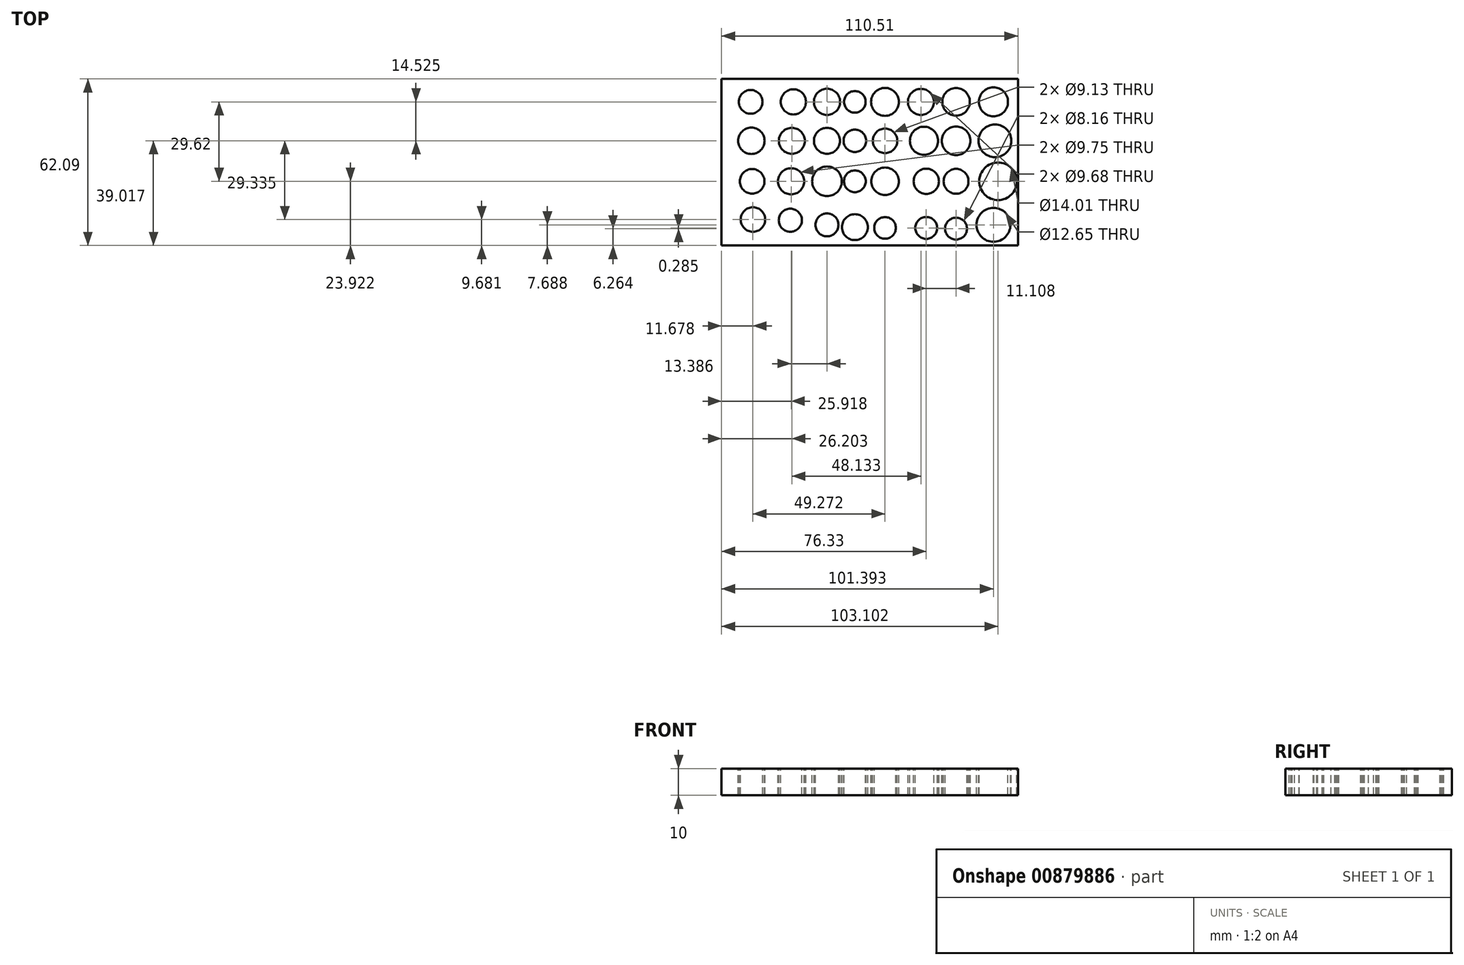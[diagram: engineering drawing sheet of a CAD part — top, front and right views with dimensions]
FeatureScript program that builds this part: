
annotation { "Feature Type Name" : "Feature", "Feature Type Description" : "" }
export const myFeature = defineFeature(function(context is Context, id is Id, definition is map)
    precondition{}
    {
        {
            var Q0;
            Q0=qCreatedBy(makeId("Top.planeOp"),FACE);
            var sketch = newSketch(context, id + "F0", { "sketchPlane" : qUnion([Q0])});
            skLineSegment(sketch, "E0.bottom", {"start": v(-49.7, 35.32) * mm, "end": v(60.8, 35.32) * mm});
            skLineSegment(sketch, "E0.top", {"start": v(-49.7, -26.77) * mm, "end": v(60.8, -26.77) * mm});
            skLineSegment(sketch, "E0.left", {"start": v(-49.7, 35.32) * mm, "end": v(-49.7, -26.77) * mm});
            skLineSegment(sketch, "E0.right", {"start": v(60.8, 35.32) * mm, "end": v(60.8, -26.77) * mm});
            skSolve(sketch);
        }
        {
            var Q0;
            Q0 = qSketchRegion(id + "F0", true);
            extrude(context, id + "F1", {"entities" : qUnion([Q0]), "depth" : 10 * mm, "offsetDistance" : 25 * mm});
        }
        {
            var Q0;
            Q0=makeQuery(id+"F1.opExtrude","CAP_FACE",FACE,{"disambiguationData":[OSD([sQuery(id+"F0.wireOp",EDGE,"E0.bottom"),sQuery(id+"F0.wireOp",EDGE,"E0.top"),sQuery(id+"F0.wireOp",EDGE,"E0.left"),sQuery(id+"F0.wireOp",EDGE,"E0.right")])],"isStart":false});
            var sketch = newSketch(context, id + "F2", { "sketchPlane" : qUnion([Q0])});
            skCircle(sketch, "E1", {"center": v(-38.88, 26.77) * mm, "radius": 4.42 * mm});
            skCircle(sketch, "E2", {"center": v(-38.6, 12.25) * mm, "radius": 4.92 * mm});
            skCircle(sketch, "E3", {"center": v(-38.3, -2.85) * mm, "radius": 4.6 * mm});
            skCircle(sketch, "E4", {"center": v(-38.02, -17.09) * mm, "radius": 4.57 * mm});
            skCircle(sketch, "E5", {"center": v(-24.07, -17.37) * mm, "radius": 4.3 * mm});
            skCircle(sketch, "E6", {"center": v(-23.78, -2.85) * mm, "radius": 4.88 * mm});
            skCircle(sketch, "E7", {"center": v(-23.5, 12.25) * mm, "radius": 4.84 * mm});
            skCircle(sketch, "E8", {"center": v(-22.93, 26.77) * mm, "radius": 4.7 * mm});
            skCircle(sketch, "E9", {"center": v(-10.4, 26.77) * mm, "radius": 4.88 * mm});
            skCircle(sketch, "E10", {"center": v(0, 26.77) * mm, "radius": 4.02 * mm});
            skCircle(sketch, "E11", {"center": v(11.25, 26.77) * mm, "radius": 5.2 * mm});
            skCircle(sketch, "E12", {"center": v(24.64, 26.77) * mm, "radius": 4.84 * mm});
            skCircle(sketch, "E13", {"center": v(37.74, 26.77) * mm, "radius": 5.13 * mm});
            skCircle(sketch, "E14", {"center": v(51.7, 26.77) * mm, "radius": 5.41 * mm});
            skCircle(sketch, "E15", {"center": v(-10.4, 12.25) * mm, "radius": 4.85 * mm});
            skCircle(sketch, "E16", {"center": v(-10.4, -2.85) * mm, "radius": 5.53 * mm});
            skCircle(sketch, "E17", {"center": v(-10.4, -19.08) * mm, "radius": 4.28 * mm});
            skCircle(sketch, "E18", {"center": v(0, 12.25) * mm, "radius": 4.19 * mm});
            skCircle(sketch, "E19", {"center": v(0, -2.85) * mm, "radius": 4.05 * mm});
            skCircle(sketch, "E20", {"center": v(0, -19.94) * mm, "radius": 4.82 * mm});
            skCircle(sketch, "E21", {"center": v(11.25, 12.25) * mm, "radius": 4.57 * mm});
            skCircle(sketch, "E22", {"center": v(11.25, -2.85) * mm, "radius": 5.13 * mm});
            skCircle(sketch, "E23", {"center": v(11.25, -20.22) * mm, "radius": 4.03 * mm});
            skCircle(sketch, "E24", {"center": v(25.78, 12.25) * mm, "radius": 5.25 * mm});
            skCircle(sketch, "E25", {"center": v(26.63, -2.85) * mm, "radius": 4.71 * mm});
            skCircle(sketch, "E26", {"center": v(26.63, -20.22) * mm, "radius": 4.08 * mm});
            skCircle(sketch, "E27", {"center": v(37.74, 12.25) * mm, "radius": 5.32 * mm});
            skCircle(sketch, "E28", {"center": v(37.74, -2.85) * mm, "radius": 4.64 * mm});
            skCircle(sketch, "E29", {"center": v(37.74, -20.5) * mm, "radius": 4.08 * mm});
            skCircle(sketch, "E30", {"center": v(52.26, 12.25) * mm, "radius": 6.12 * mm});
            skCircle(sketch, "E31", {"center": v(53.4, -2.85) * mm, "radius": 7 * mm});
            skCircle(sketch, "E32", {"center": v(51.7, -19.08) * mm, "radius": 6.32 * mm});
            skSolve(sketch);
        }
        {
            var Q0;
            Q0 = qSketchRegion(id + "F2", true);
            extrude(context, id + "F3", {"entities" : qUnion([Q0]), "operationType" : NewBodyOperationType.REMOVE, "oppositeDirection" : true, "depth" : 25 * mm, "offsetDistance" : 25 * mm});
        }
    });
